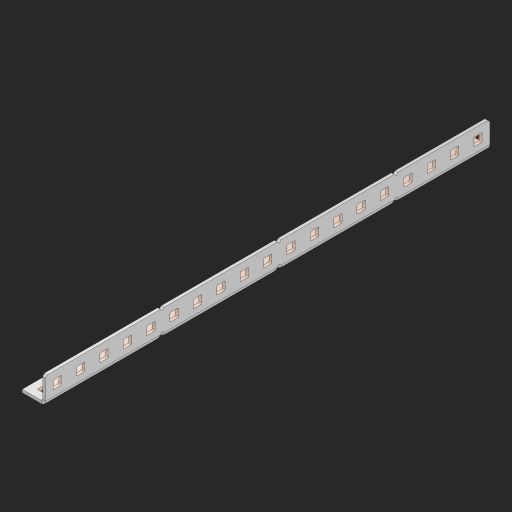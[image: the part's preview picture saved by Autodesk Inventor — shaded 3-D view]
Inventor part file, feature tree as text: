
AUTODESK INVENTOR PART (.ipt)
format: ipt  version: 2023 (Build 270158000, 158)  size: 743,424 bytes
history: native  units: in
note: dims shown in document units (in); Inventor stores cm internally (conversion verified against a paired STEP export)
features: other x43, extrude x37, sheet_metal_op x10, sketch x8, mirror x1, pattern_linear x1, chamfer x1
ambient origin geometry x8: Origin, YZ Plane, XZ Plane, XY Plane, X Axis, Y Axis, Z Axis, Center Point
bodies: Solid1 (feature_tree), Body (feature_tree)
feature tree (101):
  other  "Flange Pattern Plane"
  sheet_metal_op  "Flange Pattern"
  sheet_metal_op  "Body Pattern"
  other  "Arc Length"
  mirror  "Notch Mirror"
  pattern_linear  "Notch Pattern"  Spacing1=0.25in  [1 undecoded]
  chamfer  "End Chamfer"
  extrude  "Half Cut"  Depth=0.0625in
  sketch  "Sketch1"  dims[d0=1.5in]
  other  "Plate1"
  sketch  "Sketch2"  dims[d1=9.5in]
  other  "Plate2"
  sheet_metal_op  "Bend1"
  sheet_metal_op  "Corner1"
  sketch  "Sketch3"  dims[d2=0.0625in]
  other  "Flange Pattern Sketch"
  sketch  "Sketch7"  dims[d3=0.0625in]
  other  "Srf1"
  other  "Srf2"
  sketch  "Sketch8"  dims[d4=0.0312in]
  sketch  "Sketch9"  dims[d5=0.125in]
  other  "Srf91"
  sheet_metal_op  "Body Pattern Sketch"
  other  "Srf92"
  sketch  "Sketch13"  dims[d6=0.0625in]
  sketch  "Sketch14"  dims[d7=0.5in d8=90.0deg d9=0.0312in d10=0.25in d11=0.0625in d12=0.0625in d16=0.182in d17=0.02in d18=0.0625in d19=0.0in d20=0.25in d21=0.25in d46=0.172in d47=1.0in d48=0.0in d49=0.182in d50=0.02in d51=0.25in d52=0.25in d53=0.0625in d54=0.0in d55=0.172in d56=1.0in d57=0.0in d60=7.4803in d62=0.5in d63=0.3937in d65=0.5in d85=0.1473in d86=0.1782in d88=0.04in d89=0.0625in d90=0.0in d91=0.04in d92=0.0491in d95=2.5in d96=0.04in d97=0.25in d98=45.0deg d101=0.0in d102=2.497in d131=0.5in d132=7.4803in d134=0.5in d139=0.5in]
  other  "Srf856"
  other  "Srf1310"
  other  "Srf1311"
  other  "Srf1312"
  other  "Srf1376"
  other  "Srf1377"
  other  "Srf1728"
  other  "Srf1755"
  other  "Srf1878"
  other  "Srf1879"
  other  "Srf1880"
  other  "Srf1881"
  other  "Srf1882"
  other  "Srf1883"
  other  "Srf1884"
  other  "Srf1885"
  other  "Srf1886"
  other  "Srf1887"
  other  "Srf1888"
  other  "Srf1889"
  other  "Srf1890"
  other  "Srf1942"
  other  "Srf1943"
  other  "Srf1944"
  other  "Srf1945"
  other  "Srf1946"
  other  "Srf1947"
  other  "Srf1948"
  other  "Srf1949"
  other  "Srf1950"
  other  "Srf1951"
  other  "Srf1952"
  other  "Srf1953"
  other  "Srf1954"
  sheet_metal_op  "Flange Stamp"
  sheet_metal_op  "Flange Circle"
  sheet_metal_op  "Body Stamp"
  sheet_metal_op  "Body Circle"
  sheet_metal_op  "Notch"
  extrude  "ExtrusionSrf2"  Depth=0.0625in
  extrude  "ExtrusionSrf92"  Depth=0.5in
  extrude  "ExtrusionSrf856"  Depth=0.02in
  extrude  "ExtrusionSrf1310"  Depth=0.0625in
  extrude  "ExtrusionSrf1311"  TaperAngle=0.0deg  [1 undecoded]
  extrude  "ExtrusionSrf1312"  Depth=0.5in
  extrude  "ExtrusionSrf1376"  Depth=0.5in
  extrude  "ExtrusionSrf1377"  Depth=0.5in
  extrude  "ExtrusionSrf1728"  Depth=0.5in TaperAngle=0.0deg
  extrude  "ExtrusionSrf1755"  Depth=0.5in
  extrude  "ExtrusionSrf1878"  Depth=0.02in
  extrude  "ExtrusionSrf1879"  Depth=0.5in
  extrude  "ExtrusionSrf1880"  Depth=0.5in
  extrude  "ExtrusionSrf1881"  Depth=0.0625in
  extrude  "ExtrusionSrf1882"  TaperAngle=0.0deg  [1 undecoded]
  extrude  "ExtrusionSrf1883"  Depth=0.5in
  extrude  "ExtrusionSrf1884"  Depth=0.5in TaperAngle=0.0deg
  extrude  "ExtrusionSrf1885"  Depth=0.5in
  extrude  "ExtrusionSrf1886"  Depth=0.5in
  extrude  "ExtrusionSrf1887"  Depth=0.5in
  extrude  "ExtrusionSrf1888"  Depth=0.5in
  extrude  "ExtrusionSrf1889"  Depth=0.5in
  extrude  "ExtrusionSrf1890"  Depth=0.0625in
  extrude  "ExtrusionSrf1942"  TaperAngle=0.0deg  [1 undecoded]
  extrude  "ExtrusionSrf1943"  Depth=0.5in
  extrude  "ExtrusionSrf1944"  Depth=0.5in
  extrude  "ExtrusionSrf1945"  Depth=0.5in
  extrude  "ExtrusionSrf1946"  Depth=0.5in TaperAngle=45.0deg
  extrude  "ExtrusionSrf1947"  TaperAngle=0.0deg  [1 undecoded]
  extrude  "ExtrusionSrf1948"  Depth=0.5in
  extrude  "ExtrusionSrf1949"  Depth=0.5in
  extrude  "ExtrusionSrf1950"  Depth=0.5in
  extrude  "ExtrusionSrf1951"  Depth=0.5in
  extrude  "ExtrusionSrf1952"  Depth=0.5in
  extrude  "ExtrusionSrf1953"  [1 undecoded]
  extrude  "ExtrusionSrf1954"  [1 undecoded]
note: 7 required parameter values undecoded (feature->parameter linkage not recoverable at this tier; creation-order binding heuristic only, values carry confidence <= 0.55)
